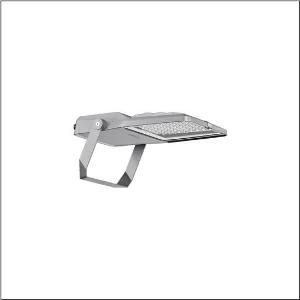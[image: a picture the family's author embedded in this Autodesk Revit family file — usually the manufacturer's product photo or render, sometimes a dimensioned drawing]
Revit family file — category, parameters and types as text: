
# Revit family: floodlight_fl_21_iq_mini___pl61_5xa7772b1c1a_06a2
name_source: partatom
category: Lighting Fixtures
units: mm (PartAtom-declared; Revit-internal decimal feet)

## family parameters
Cut with Voids When Loaded = No
Host = Face
Light Source = No
Part Type = Normal
Room Calculation Point = No
Round Connector Dimension = Use Diameter
Shared = No

## types (1)
- --- (1 x LED, 5080 lm, 45.5 W, 2200K)
    Apparent Load = 46 VA
    CIE Flux Codes = 33 65 98 100 100
    Color Rendering = 70
    Color Temperature = 2200K
    Default Elevation = 1800 mm
    Description = Floodlight FL 21 iQ mini, floodlight, primary light control with lens, of PMMA, primary optical cover: protective disc, of toughened safety glass, transparent, light distribution: PL61, light emission: direct distribution, installation type: surface-mounted, lamps: LED, High Power LED, rated values: 5.080lm | 45,5W | 111,6lm/W (begin service life); end service life: 5.080lm | 48W; at 50% lumin. flux: 2.540lm | 21,4W | 118,7lm/W, colour temperature: 2200K, colour rendering: CRI > 70, light colour: 722, light setting 1 begin service life: 100% | 5.080lm | 45,5W | 111,6lm/W | 2.200K, light setting 1 end service life: 48W, further light settings possible, control: Street-Remote, Auto-Match, Temp-Guard, Night-Set, Smart-Wire, Desk-Remote (wireless, voltage-free reading and setting of iQ features in the workshop via application-optimized NFC function/RFID function), optimised constant luminous flux control (CLO 2.0), pre-setting: linear dimming characteristic, with terminal, 6-pole, mains connection: 220..240V, AC, 50/60Hz, luminaire housing, of diecast aluminium, powder-coated, SITECO metallic grey (DB 702S), corrosivity category C5 mid according to DIN EN ISO 12944suitable for swimming poolschlorine-resistant, sealing non-destructively replaceable, mounting bracket, of steel, galvanised, powder-coated, SITECO metallic grey (DB 702S), protection rating (complete): IP66, insulation class (complete): insulation class II (safety insulation), certification: CE, ENEC, VDE, protection symbol: D, impact resistance: IK08, permissible operating ambient temperature: -40..+40°C, permissible operating ambient temperature for outdoor applications: -40..+50°C, standard: DIN EN 12944, LABS conformity tested according to VDMA 24364:2018-05, packaging unit: 1 piece

Light Distribution: PL61
    Height = 70 mm
    Lamp = 1 x LED
    Lamp Light Flux = 5080 lm
    Lamp Power = 45.5 W
    Lamp count = 1
    Length = 485 mm
    Luminous efficacy = 112 lm/W
    Manufacturer = Siteco
    ModVariant = No
    Model = 5XA7772B1C1A
    Mounting Place = Pole
    Mounting Type = Pole annexe
    Number of Poles = 1
    OnlyDefault = Yes
    Power Factor = 1
    Product Name = Floodlight FL 21 iQ mini | PL61
    Product group = floodlight | pylon annexe
    ProductGroupID = 6201
    Protection Class = Protection class II
    Protection Degree = IP 66
    RLX_Detail_Level = 1
    RLX_Emergency_Light_Flux = 0 lm
    RLX_Emergency_Type = 0
    RLX_Emergency_Type_DB = No
    RlxData = <blob elided: 96449 chars, md5=3befd585>
    Socket = socket
    Standby Power = 0 W
    System Light Flux = 5080 lm
    System Power = 46 W
    Type Comments = factory setting: luminous flux: 100 % | dim-lin: 254 | 463 mA
    Type Image = l_1006845.jpg
    URL = http://relux.com
    VarID = @adj_174733
    Voltage = 0 V
    Weight = 0.00 kg
    Width = 337 mm

## geometry (parser evidence)
native form markers: Blend x4, Sweep x12
no freeform markers — native parametric forms only
